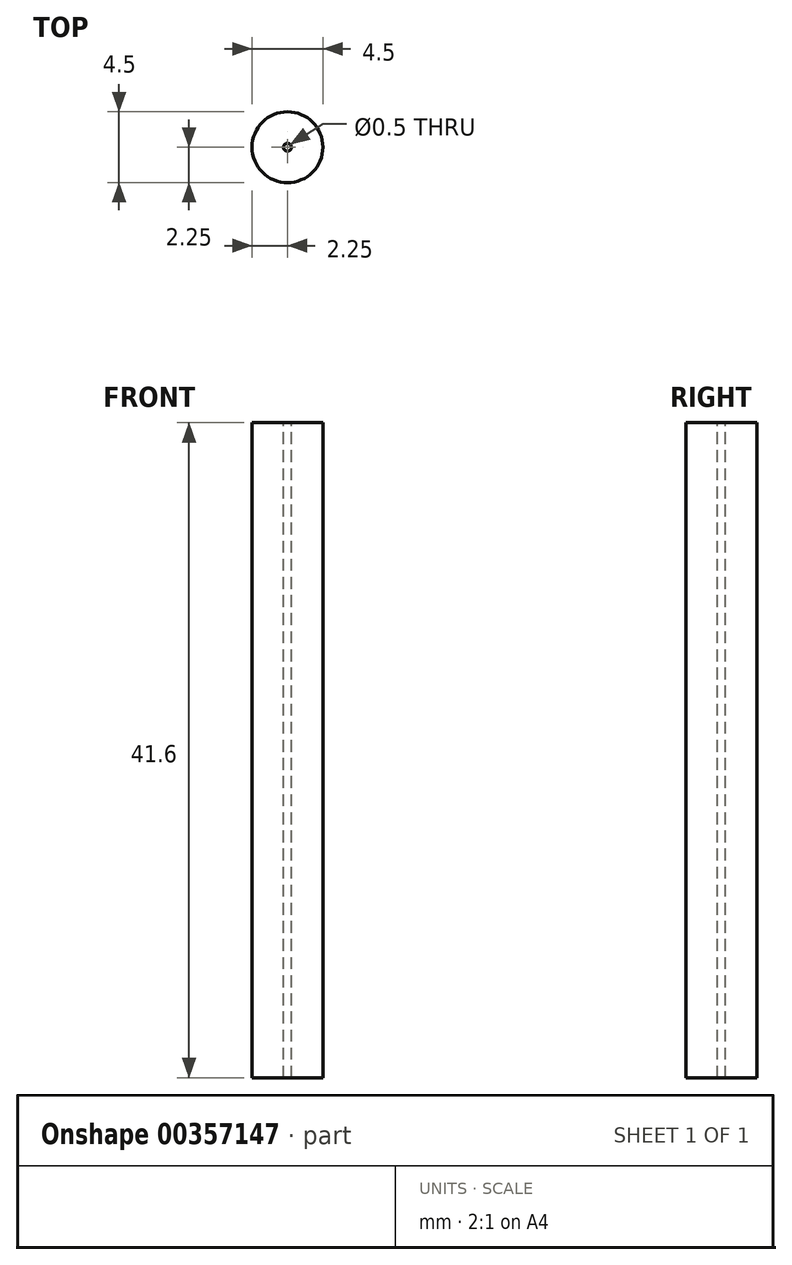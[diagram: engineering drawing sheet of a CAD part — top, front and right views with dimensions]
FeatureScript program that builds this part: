
annotation { "Feature Type Name" : "Feature", "Feature Type Description" : "" }
export const myFeature = defineFeature(function(context is Context, id is Id, definition is map)
    precondition{}
    {
        {
            var Q0;
            Q0=qCreatedBy(makeId("Top.planeOp"),FACE);
            var sketch = newSketch(context, id + "F0", { "sketchPlane" : qUnion([Q0])});
            skCircle(sketch, "E0", {"center": v(0, 0) * mm, "radius": 0.25 * mm});
            skCircle(sketch, "E1", {"center": v(0, 0) * mm, "radius": 2 * mm});
            skCircle(sketch, "E2", {"center": v(0, 0) * mm, "radius": 2.25 * mm});
            skSolve(sketch);
        }
        {
            var Q0;
            Q0=makeQuery(id+"F0.imprint","IMPRINT",FACE,{"disambiguationData":[TD([[makeQuery(id+"F0.imprint","IMPRINT",EDGE,{"derivedFrom":sQuery(id+"F0.wireOp",EDGE,"E1")}),-1.0]])]});
            var Q1;
            Q1=makeQuery(id+"F0.imprint","IMPRINT",FACE,{"disambiguationData":[TD([[makeQuery(id+"F0.imprint","IMPRINT",EDGE,{"derivedFrom":sQuery(id+"F0.wireOp",EDGE,"E0")}),-1.0]])]});
            extrude(context, id + "F1", {"entities" : qUnion([Q0, Q1]), "endBound" : BoundingType.SYMMETRIC, "oppositeDirection" : true, "depth" : 41.6 * mm});
        }
    });
